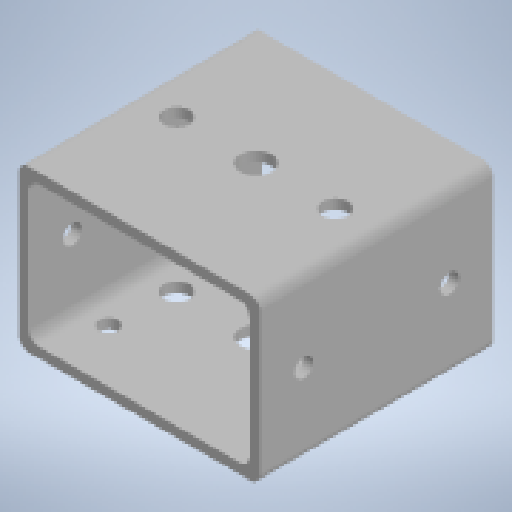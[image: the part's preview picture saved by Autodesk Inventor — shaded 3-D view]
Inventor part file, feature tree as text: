
AUTODESK INVENTOR PART (.ipt)
format: ipt  version: 2023 (Build 270158000, 158)  size: 203,776 bytes
history: native  units: in
note: dims shown in document units (in); Inventor stores cm internally (conversion verified against a paired STEP export)
features: extrude x5, sketch x4, shell x1, fillet x1, projected_geometry x1
ambient origin geometry x8: Origin, YZ Plane, XZ Plane, XY Plane, X Axis, Y Axis, Z Axis, Center Point
bodies: Solid1 (feature_tree)
feature tree (12):
  extrude  "Extrusion1"  Depth=2.0in
  shell  "Shell1"  Thickness=2.9in
  extrude  "Extrusion2"  Depth=0.125in
  extrude  "Extrusion3"  Depth=1.5748in
  fillet  "Fillet1"  Radius=0.9375in
  extrude  "Extrusion4"  Depth=3.0in TaperAngle=0.0deg
  extrude  "Extrusion5"  Depth=0.125in
  sketch  "Sketch1"  dims[d0=3.0in d1=2.0in d2=2.9in d3=0.0in]
  sketch  "Sketch2"  dims[d4=0.125in d5=0.2362in]
  sketch  "Sketch4"  dims[d6=2.0866in d7=1.5748in d8=0.9375in d9=0.0in]
  sketch  "Sketch5"  dims[d10=0.315in d11=4.0in d12=0.0in d13=0.125in d14=0.315in d15=3.0in d16=0.0in d17=0.2362in d18=1.811in d19=1.0in d20=0.0in d22=1.9685in]
  projected_geometry  "Projected Loop1"
